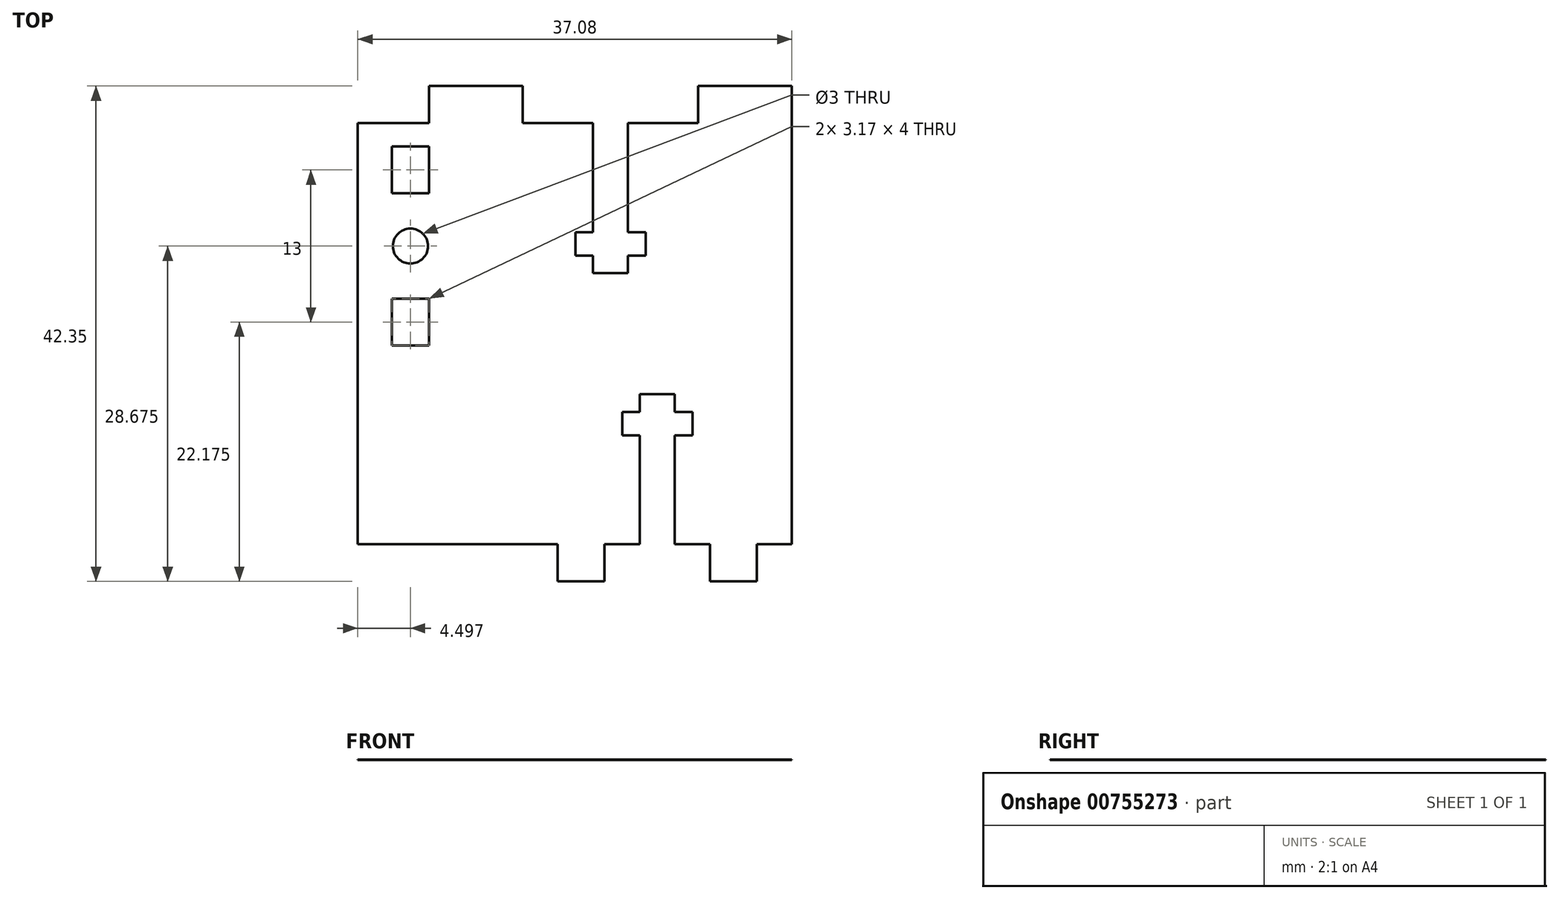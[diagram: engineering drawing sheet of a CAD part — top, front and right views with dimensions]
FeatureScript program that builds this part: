
annotation { "Feature Type Name" : "Feature", "Feature Type Description" : "" }
export const myFeature = defineFeature(function(context is Context, id is Id, definition is map)
    precondition{}
    {
        {
            var Q0;
            Q0=qCreatedBy(makeId("Top.planeOp"),FACE);
            var sketch = newSketch(context, id + "F0", { "sketchPlane" : qUnion([Q0])});
            skLineSegment(sketch, "E0.top", {"start": v(8.15, 23.97) * mm, "end": v(11.15, 23.97) * mm});
            skLineSegment(sketch, "E0.left", {"start": v(8.15, 36.8) * mm, "end": v(8.15, 27.47) * mm});
            skLineSegment(sketch, "E0.right", {"start": v(11.15, 36.8) * mm, "end": v(11.15, 27.47) * mm});
            skPoint(sketch, "E0.middle", {"position": v(9.65, 31.97) * mm});
            skLineSegment(sketch, "E1.bottom", {"start": v(6.65, 27.47) * mm, "end": v(8.15, 27.47) * mm});
            skLineSegment(sketch, "E1.top", {"start": v(6.65, 25.47) * mm, "end": v(8.15, 25.47) * mm});
            skLineSegment(sketch, "E1.left", {"start": v(6.65, 27.47) * mm, "end": v(6.65, 25.47) * mm});
            skLineSegment(sketch, "E1.right", {"start": v(12.65, 27.47) * mm, "end": v(12.65, 25.47) * mm});
            skPoint(sketch, "E1.middle", {"position": v(9.65, 26.47) * mm});
            skLineSegment(sketch, "E2.bottom", {"start": v(25.15, 39.97) * mm, "end": v(17.15, 39.97) * mm});
            skLineSegment(sketch, "E2.left", {"start": v(25.15, 39.97) * mm, "end": v(25.15, 36.8) * mm});
            skLineSegment(sketch, "E2.right", {"start": v(17.15, 39.97) * mm, "end": v(17.15, 36.8) * mm});
            skLineSegment(sketch, "E3.MirrorCS", {"start": v(2.15, 39.97) * mm, "end": v(2.15, 36.8) * mm});
            skLineSegment(sketch, "E4.MirrorCS", {"start": v(-5.85, 39.97) * mm, "end": v(2.15, 39.97) * mm});
            skLineSegment(sketch, "E5.MirrorCS", {"start": v(-5.85, 39.97) * mm, "end": v(-5.85, 36.8) * mm});
            skLineSegment(sketch, "E6", {"start": v(2.15, 36.8) * mm, "end": v(8.15, 36.8) * mm});
            skLineSegment(sketch, "E7.bottom", {"start": v(12.15, 13.62) * mm, "end": v(15.15, 13.62) * mm});
            skLineSegment(sketch, "E7.left", {"start": v(12.15, 13.62) * mm, "end": v(12.15, 12.12) * mm});
            skLineSegment(sketch, "E7.right", {"start": v(15.15, 13.62) * mm, "end": v(15.15, 12.12) * mm});
            skPoint(sketch, "E7.middle", {"position": v(13.65, 5.62) * mm});
            skLineSegment(sketch, "E8.bottom", {"start": v(10.65, 12.12) * mm, "end": v(12.15, 12.12) * mm});
            skLineSegment(sketch, "E8.top", {"start": v(10.65, 10.12) * mm, "end": v(12.15, 10.12) * mm});
            skLineSegment(sketch, "E8.left", {"start": v(10.65, 12.12) * mm, "end": v(10.65, 10.12) * mm});
            skLineSegment(sketch, "E8.right", {"start": v(16.65, 12.12) * mm, "end": v(16.65, 10.12) * mm});
            skPoint(sketch, "E8.middle", {"position": v(13.65, 11.12) * mm});
            skLineSegment(sketch, "E9.bottom", {"start": v(18.15, -2.38) * mm, "end": v(22.15, -2.38) * mm});
            skLineSegment(sketch, "E9.left", {"start": v(18.15, -2.38) * mm, "end": v(18.15, 0.8) * mm});
            skLineSegment(sketch, "E9.right", {"start": v(22.15, -2.38) * mm, "end": v(22.15, 0.8) * mm});
            skLineSegment(sketch, "E10.MirrorCS", {"start": v(9.15, -2.38) * mm, "end": v(9.15, 0.8) * mm});
            skLineSegment(sketch, "E11.MirrorCS", {"start": v(5.15, -2.38) * mm, "end": v(5.15, 0.8) * mm});
            skLineSegment(sketch, "E12.MirrorCS", {"start": v(9.15, -2.38) * mm, "end": v(5.15, -2.38) * mm});
            skCircle(sketch, "E13", {"center": v(-7.43, 26.3) * mm, "radius": 1.5 * mm});
            skLineSegment(sketch, "E14.bottom", {"start": v(-9.02, 34.8) * mm, "end": v(-5.85, 34.8) * mm});
            skLineSegment(sketch, "E14.top", {"start": v(-9.02, 30.8) * mm, "end": v(-5.85, 30.8) * mm});
            skLineSegment(sketch, "E14.left", {"start": v(-9.02, 34.8) * mm, "end": v(-9.02, 30.8) * mm});
            skLineSegment(sketch, "E14.right", {"start": v(-5.85, 34.8) * mm, "end": v(-5.85, 30.8) * mm});
            skPoint(sketch, "E14.middle", {"position": v(-7.43, 32.8) * mm});
            skLineSegment(sketch, "E15.MirrorCS", {"start": v(-5.85, 17.8) * mm, "end": v(-5.85, 21.8) * mm});
            skLineSegment(sketch, "E16.MirrorCS", {"start": v(-9.02, 21.8) * mm, "end": v(-5.85, 21.8) * mm});
            skLineSegment(sketch, "E17.MirrorCS", {"start": v(-9.02, 17.8) * mm, "end": v(-9.02, 21.8) * mm});
            skLineSegment(sketch, "E18.MirrorCS", {"start": v(-9.02, 17.8) * mm, "end": v(-5.85, 17.8) * mm});
            skLineSegment(sketch, "E19", {"start": v(-5.85, 36.8) * mm, "end": v(-11.93, 36.8) * mm});
            skLineSegment(sketch, "E20", {"start": v(-11.93, 36.8) * mm, "end": v(-11.93, 0.8) * mm});
            skLineSegment(sketch, "E21", {"start": v(25.15, 36.8) * mm, "end": v(25.15, 0.8) * mm});
            skLineSegment(sketch, "E22", {"start": v(-11.93, 0.8) * mm, "end": v(5.15, 0.8) * mm});
            skPoint(sketch, "E23.orphan", {"position": v(-5.85, 38.38) * mm});
            skPoint(sketch, "E24.end.orphan", {"position": v(25.15, 38.38) * mm});
            skPoint(sketch, "E25.orphan", {"position": v(11.15, 39.97) * mm});
            skPoint(sketch, "E26.orphan", {"position": v(8.15, 39.97) * mm});
            skLineSegment(sketch, "E27.trimOffspring", {"start": v(11.15, 36.8) * mm, "end": v(17.15, 36.8) * mm});
            skLineSegment(sketch, "E28.trimOffspring", {"start": v(11.15, 27.47) * mm, "end": v(12.65, 27.47) * mm});
            skLineSegment(sketch, "E29.trimOffspring", {"start": v(11.15, 25.47) * mm, "end": v(11.15, 23.97) * mm});
            skLineSegment(sketch, "E30.trimOffspring", {"start": v(8.15, 25.47) * mm, "end": v(8.15, 23.97) * mm});
            skLineSegment(sketch, "E31.trimOffspring", {"start": v(11.15, 25.47) * mm, "end": v(12.65, 25.47) * mm});
            skLineSegment(sketch, "E32.trimOffspring", {"start": v(15.15, 12.12) * mm, "end": v(16.65, 12.12) * mm});
            skLineSegment(sketch, "E33.trimOffspring", {"start": v(15.15, 10.12) * mm, "end": v(15.15, 0.8) * mm});
            skLineSegment(sketch, "E34.trimOffspring", {"start": v(12.15, 10.12) * mm, "end": v(12.15, 0.8) * mm});
            skLineSegment(sketch, "E35.trimOffspring", {"start": v(15.15, 10.12) * mm, "end": v(16.65, 10.12) * mm});
            skPoint(sketch, "E36.start.orphan", {"position": v(5.15, -0.8) * mm});
            skPoint(sketch, "E37.trimOffspring.end.orphan", {"position": v(22.15, -0.8) * mm});
            skLineSegment(sketch, "E38.trimOffspring", {"start": v(15.15, 0.8) * mm, "end": v(18.15, 0.8) * mm});
            skPoint(sketch, "E7.top.end.orphan", {"position": v(15.15, -2.38) * mm});
            skPoint(sketch, "E7.top.start.orphan", {"position": v(12.15, -2.38) * mm});
            skLineSegment(sketch, "E39.trimOffspring", {"start": v(9.15, 0.8) * mm, "end": v(12.15, 0.8) * mm});
            skLineSegment(sketch, "E40.trimOffspring", {"start": v(22.15, 0.8) * mm, "end": v(25.15, 0.8) * mm});
            skSolve(sketch);
        }
        {
            var Q0;
            {var subQ24=sQuery(id+"F0.wireOp",EDGE,"E0.top");Q0=makeQuery(id+"F0.imprint","IMPRINT",FACE,{"disambiguationData":[TD([[makeQuery(id+"F0.imprint","IMPRINT",EDGE,{"derivedFrom":subQ24}),-1.0]])]});}
            var Q1;
            Q1=makeQuery(id+"F0.imprint","IMPRINT",FACE,{"disambiguationData":[TD([[makeQuery(id+"F0.imprint","IMPRINT",EDGE,{"derivedFrom":sQuery(id+"F0.wireOp",EDGE,"E3.MirrorCS")}),-1.0]])]});
            var Q2;
            Q2=makeQuery(id+"F0.imprint","IMPRINT",FACE,{"disambiguationData":[TD([[makeQuery(id+"F0.imprint","IMPRINT",EDGE,{"derivedFrom":sQuery(id+"F0.wireOp",EDGE,"E2.bottom")}),1.0]])]});
            var Q3;
            Q3=makeQuery(id+"F0.imprint","IMPRINT",FACE,{"disambiguationData":[TD([[makeQuery(id+"F0.imprint","IMPRINT",EDGE,{"derivedFrom":sQuery(id+"F0.wireOp",EDGE,"E9.bottom")}),1.0]])]});
            var Q4;
            {var subQ0=sQuery(id+"F0.wireOp",EDGE,"E10.MirrorCS");Q4=makeQuery(id+"F0.imprint","IMPRINT",FACE,{"disambiguationData":[TD([[makeQuery(id+"F0.imprint","IMPRINT",EDGE,{"derivedFrom":subQ0}),1.0]])]});}
            var Q5;
            {var subQ0=sQuery(id+"F0.wireOp",EDGE,"E2.top");Q5=makeQuery(id+"F0.imprint","IMPRINT",FACE,{"disambiguationData":[TD([[makeQuery(id+"F0.imprint","IMPRINT",EDGE,{"derivedFrom":subQ0}),-1.0]])]});}
            var Q6;
            {var subQ0=sQuery(id+"F0.wireOp",EDGE,"E22");var subQ1=sQuery(id+"F0.wireOp",EDGE,"E9.left");var subQ2=makeQuery(id+"F0.imprint","INTERSECT",VERTEX,{"derivedFrom":[subQ1,subQ0]});Q6=makeQuery(id+"F0.imprint","IMPRINT",FACE,{"disambiguationData":[TD([[makeQuery(id+"F0.imprint","IMPRINT",EDGE,{"disambiguationData":[TD([[subQ2,1.0]])],"derivedFrom":subQ1}),-1.0]])]});}
            extrude(context, id + "F1", {"entities" : qUnion([Q0, Q1, Q2, Q3, Q4, Q5, Q6]), "depth" : 1 / 203.2 * mm, "offsetDistance" : 25 * mm});
        }
    });
